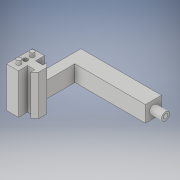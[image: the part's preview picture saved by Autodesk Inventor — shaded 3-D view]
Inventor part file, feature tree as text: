
AUTODESK INVENTOR PART (.ipt)
format: ipt  version: 2018 (Build 220112000, 112)  size: 164,352 bytes
history: native  units: in
note: dims shown in document units (in); Inventor stores cm internally (conversion verified against a paired STEP export)
features: sketch x7, extrude x5, hole x2
ambient origin geometry x8: Origin, YZ Plane, XZ Plane, XY Plane, X Axis, Y Axis, Z Axis, Center Point
bodies: Solid1 (feature_tree)
feature tree (14):
  extrude  "Extrusion1"  Depth=0.65in
  extrude  "Extrusion2"  Depth=0.28in
  hole  "Hole1"  [1 undecoded]
  extrude  "Extrusion3"  Depth=0.1in
  extrude  "Extrusion4"  Depth=1.0in
  extrude  "Extrusion5"  Depth=0.11in
  hole  "Hole2"  [1 undecoded]
  sketch  "Sketch1"  dims[d0=0.3in d1=0.65in]
  sketch  "Sketch2"  dims[d2=0.225in d3=0.28in]
  sketch  "Sketch3"  dims[d4=0.2in d5=0.1in]
  sketch  "Sketch4"  dims[d6=0.1in d7=0.1in]
  sketch  "Sketch5"  dims[d8=1.0in d9=0.0in d10=0.16in]
  sketch  "Sketch6"  dims[d11=0.16in d12=0.11in]
  sketch  "Sketch7"  dims[d13=0.11in d14=0.1in d15=0.0in d16=0.325in d17=0.11in d18=0.75in d19=0.375in d20=0.25in d21=0.5635in d22=0.45in d23=0.8108in d24=0.25in d25=0.4in d26=1.2in d27=0.0in d28=0.4in d29=1.75in d30=0.0in d31=0.2in d32=0.2in d33=0.3in d34=0.0in d35=0.11in d36=0.11in d37=0.75in d38=0.375in d39=0.25in d40=0.5635in d41=0.63in d42=0.8108in]
note: 2 required parameter values undecoded (feature->parameter linkage not recoverable at this tier; creation-order binding heuristic only, values carry confidence <= 0.55)
